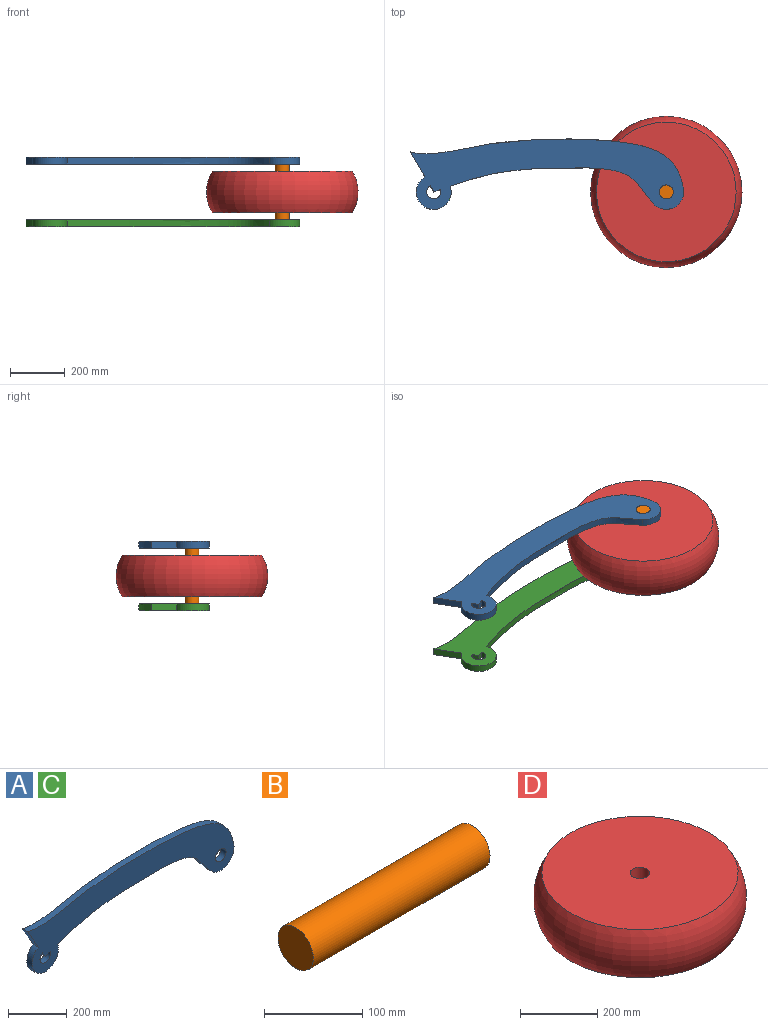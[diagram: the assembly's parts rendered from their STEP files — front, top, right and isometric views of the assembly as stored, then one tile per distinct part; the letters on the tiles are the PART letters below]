
ASSEMBLY  parts=4 mates=3
PART A: 11 faces, bbox 996x25.4x268.5 mm
  f0: plane 25.4x21.88mm, normal (-0.86,0,-0.51), area 645.2mm2, adj f1,f4,f5,f9
  f1: extruded ~25.4x23.87mm, area 645.2mm2, adj f0,f4,f5,f9
  f2: cylinder r=63.5mm len=110.52mm, axis (0,1,0), area 4334.4mm2, adj f4,f5,f6,f8
  f3: cylinder r=25.4mm len=50.8mm, axis (0,1,0), area 4053.7mm2, adj f4,f5
  f4: plane 996.02x268.54mm, normal (0,-1,0), area 122000.6mm2, adj f0,f1,f2,f3,f6,f7,f8,f9
  f5: plane 996.02x268.54mm, normal (0,1,0), area 122000.6mm2, adj f0,f1,f2,f3,f6,f7,f8,f9
  f6: extruded ~993.5x175.16mm, area 27369.3mm2, adj f2,f4,f5,f7
  f7: plane 92.08x54.29mm, normal (-0.86,0,-0.51), area 2715mm2, adj f4,f5,f6,f10
  f8: extruded ~739.2x131.19mm, area 20254.2mm2, adj f2,f4,f5,f10
  f9: cylinder r=25.4mm len=50.8mm, axis (0,1,0), area 2921.5mm2, adj f0,f1,f4,f5
  f10: cylinder r=63.5mm len=127mm, axis (0,1,0), area 7297.8mm2, adj f4,f5,f7,f8
PART B: 3 faces, bbox 254x50.8x50.8 mm
  f0: cylinder r=25.4mm len=254mm, axis (-1,0,0), area 40536.6mm2, adj f1,f2
  f1: plane 50.8x50.8mm, normal (1,0,0), area 2026.8mm2, adj f0
  f2: plane 50.8x50.8mm, normal (-1,0,0), area 2026.8mm2, adj f0
PART C: same geometry as A
PART D: 4 faces, bbox 551.1x551.1x152.4 mm
  f0: torus R=130.09mm, axis (0,0,1), area 270402.3mm2, adj f1,f2
  f1: plane 508x508mm, normal (0,0,1), area 200656.2mm2, adj f0,f3
  f2: plane 508x508mm, normal (0,0,-1), area 200656.2mm2, adj f0,f3
  f3: cylinder r=25.4mm len=152.4mm, axis (0,0,1), area 24322mm2, adj f1,f2
PLACE A rot(axis=(-1,0,0),90deg) t=(-44.74,-0.16,172.27)mm
PLACE B rot(axis=(-0.71,0,0.71),180deg) t=(-44.74,-0.16,197.67)mm
PLACE C rot(axis=(-1,0,0),90deg) t=(-44.74,-0.16,-56.33)mm
PLACE D t=(-44.74,-0.16,-5.53)mm
MATE pin_slot A.f3 <-> B.f0  axis (0,0,1) through (-44.74,-0.16,197.67)mm
MATE pin_slot B.f0 <-> D.f3  axis (0,0,1) through (-44.74,-0.16,70.67)mm
MATE pin_slot C.f3 <-> B.f0  axis (0,0,-1) through (-44.74,-0.16,-56.33)mm
